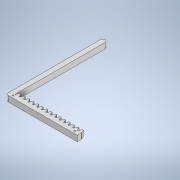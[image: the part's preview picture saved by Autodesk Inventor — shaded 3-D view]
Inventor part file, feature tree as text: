
AUTODESK INVENTOR PART (.ipt)
format: ipt  version: 2021 (Build 250183000, 183)  size: 220,672 bytes
history: native  units: in
note: dims shown in document units (in); Inventor stores cm internally (conversion verified against a paired STEP export)
features: extrude x2, fillet x1, sketch x1
ambient origin geometry x8: Origin, YZ Plane, XZ Plane, XY Plane, X Axis, Y Axis, Z Axis, Center Point
bodies: Solid1 (feature_tree), Solid2 (feature_tree)
feature tree (4):
  extrude  "Extrusion4"  Depth=0.4724in
  fillet  "Fillet3"  Radius=8.0315in
  extrude  "Extrusion7"  TaperAngle=0.0deg  [1 undecoded]
  sketch  "Sketch7"  dims[d16=0.3937in d17=0.0in d23=0.4724in d24=8.0315in d25=0.0in d29=0.1969in d30=0.1181in d31=0.1181in d32=0.3937in d33=0.1969in d34=0.1969in d35=0.3937in d36=0.0in d37=0.0in d3=0.0197in d4=1.9685in d5=0.0197in d6=1.9685in d14=0.0197in d15=1.9685in]
note: 1 required parameter value undecoded (feature->parameter linkage not recoverable at this tier; creation-order binding heuristic only, values carry confidence <= 0.55)
